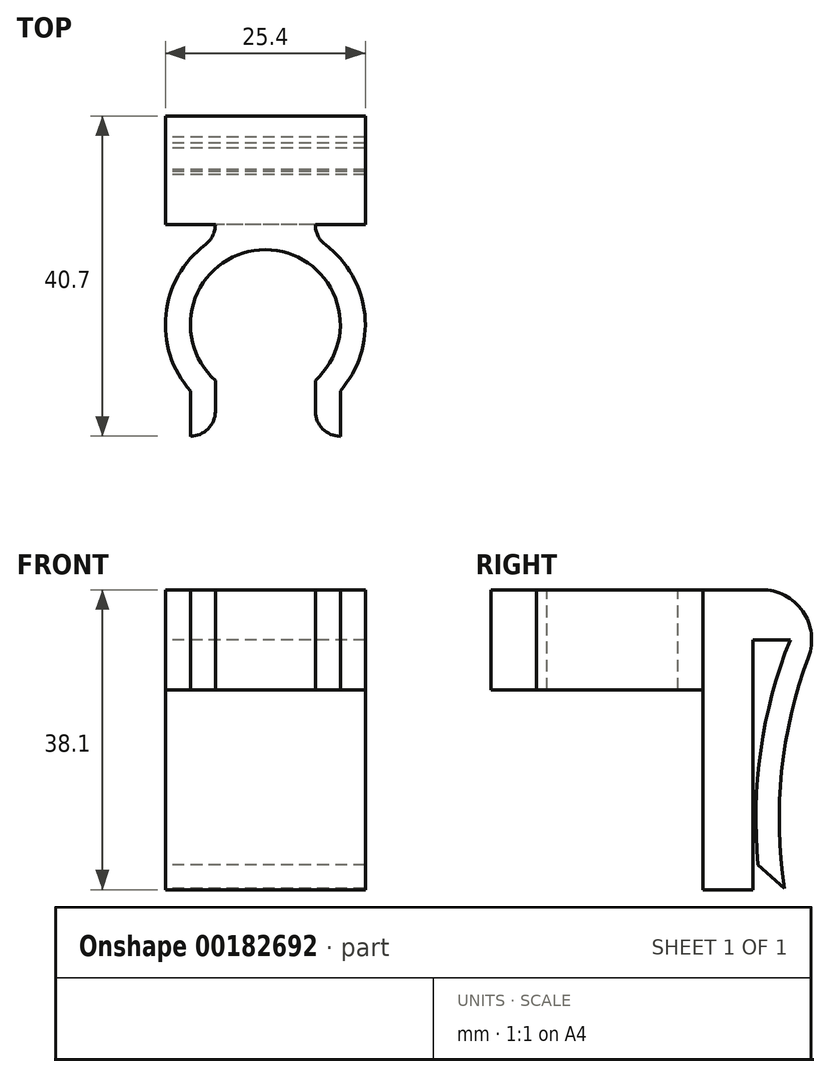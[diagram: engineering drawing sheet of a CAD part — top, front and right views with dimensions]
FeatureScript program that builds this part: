
annotation { "Feature Type Name" : "Feature", "Feature Type Description" : "" }
export const myFeature = defineFeature(function(context is Context, id is Id, definition is map)
    precondition{}
    {
        {
            var Q0;
            Q0=qCreatedBy(makeId("Right.planeOp"),FACE);
            var sketch = newSketch(context, id + "F0", { "sketchPlane" : qUnion([Q0])});
            skLineSegment(sketch, "E0", {"start": v(6.35, -44.45) * mm, "end": v(6.35, 6.35) * mm});
            skLineSegment(sketch, "E1", {"start": v(6.35, 6.35) * mm, "end": v(17.46, 6.35) * mm});
            skLineSegment(sketch, "E2", {"start": v(6.35, -44.45) * mm, "end": v(0, -44.45) * mm});
            skLineSegment(sketch, "E3", {"start": v(0, -44.45) * mm, "end": v(0, 6.35) * mm});
            skLineSegment(sketch, "E4", {"start": v(0, 6.35) * mm, "end": v(6.35, 6.35) * mm});
            skLineSegment(sketch, "E5", {"start": v(0, 0) * mm, "end": v(6.35, 0) * mm});
            skLineSegment(sketch, "E6", {"start": v(6.35, 0) * mm, "end": v(11.11, 0) * mm});
            skArc(sketch, "E7", {"start": v(11.11, 0) * mm, "mid": v(6.75, -22.19) * mm, "end": v(10.73, -44.45) * mm});
            skLineSegment(sketch, "E8", {"start": v(10.73, -44.45) * mm, "end": v(13.9, -44.45) * mm});
            skArc(sketch, "E9", {"start": v(17.46, 6.35) * mm, "mid": v(9.85, -18.64) * mm, "end": v(13.9, -44.45) * mm});
            skLineSegment(sketch, "E10", {"start": v(6.35, -44.45) * mm, "end": v(10.73, -44.45) * mm});
            skLineSegment(sketch, "E11", {"start": v(0, -31.75) * mm, "end": v(6.35, -31.75) * mm});
            skLineSegment(sketch, "E12", {"start": v(6.35, -31.75) * mm, "end": v(7.42, -31.75) * mm, "construction": true});
            skLineSegment(sketch, "E13", {"start": v(7.42, -31.75) * mm, "end": v(10.4, -31.75) * mm});
            skSolve(sketch);
        }
        {
            var Q0;
            {var subQ0=sQuery(id+"F0.wireOp",EDGE,"E4");Q0=makeQuery(id+"F0.imprint","IMPRINT",FACE,{"disambiguationData":[TD([[makeQuery(id+"F0.imprint","IMPRINT",EDGE,{"derivedFrom":subQ0}),-1.0]])]});}
            var Q1;
            {var subQ0=sQuery(id+"F0.wireOp",EDGE,"E5");Q1=makeQuery(id+"F0.imprint","IMPRINT",FACE,{"disambiguationData":[TD([[makeQuery(id+"F0.imprint","IMPRINT",EDGE,{"derivedFrom":subQ0}),-1.0]])]});}
            var Q2;
            {var subQ3=sQuery(id+"F0.wireOp",EDGE,"E1");Q2=makeQuery(id+"F0.imprint","IMPRINT",FACE,{"disambiguationData":[TD([[makeQuery(id+"F0.imprint","IMPRINT",EDGE,{"derivedFrom":subQ3}),-1.0]])]});}
            extrude(context, id + "F1", {"entities" : qUnion([Q0, Q1, Q2]), "depth" : 25.4 * mm});
        }
        {
            var Q0;
            Q0=makeQuery(id+"F1.opExtrude","SWEPT_FACE",FACE,{"disambiguationData":[OSD([sQuery(id+"F0.wireOp",EDGE,"E1"),sQuery(id+"F0.wireOp",EDGE,"E4")])]});
            var sketch = newSketch(context, id + "F2", { "sketchPlane" : qUnion([Q0])});
            skLineSegment(sketch, "E14", {"start": v(12.7, 0) * mm, "end": v(12.7, -12.7) * mm, "construction": true});
            skLineSegment(sketch, "E15", {"start": v(6.35, 0) * mm, "end": v(6.35, -1.7) * mm});
            skLineSegment(sketch, "E16", {"start": v(19.05, 0) * mm, "end": v(19.05, -1.7) * mm});
            skLineSegment(sketch, "E17", {"start": v(19.05, 0) * mm, "end": v(25.4, 0) * mm});
            skLineSegment(sketch, "E18", {"start": v(6.35, 0) * mm, "end": v(0, 0) * mm});
            skLineSegment(sketch, "E19", {"start": v(6.35, -23.7) * mm, "end": v(6.35, -26.87) * mm});
            skLineSegment(sketch, "E20", {"start": v(6.35, -26.87) * mm, "end": v(3.18, -26.87) * mm});
            skLineSegment(sketch, "E21", {"start": v(3.18, -26.87) * mm, "end": v(3.18, -21.1) * mm});
            skLineSegment(sketch, "E22.MirrorCS", {"start": v(22.23, -26.87) * mm, "end": v(22.23, -21.1) * mm});
            skLineSegment(sketch, "E23.MirrorCS", {"start": v(19.05, -23.7) * mm, "end": v(19.05, -26.87) * mm});
            skLineSegment(sketch, "E24.MirrorCS", {"start": v(19.05, -26.87) * mm, "end": v(22.23, -26.87) * mm});
            skLineSegment(sketch, "E25", {"start": v(6.35, -19.8) * mm, "end": v(6.35, -19.8) * mm});
            skLineSegment(sketch, "E26", {"start": v(6.35, -5.6) * mm, "end": v(6.35, -19.8) * mm, "construction": true});
            skLineSegment(sketch, "E27", {"start": v(6.35, -1.7) * mm, "end": v(6.35, -5.6) * mm, "construction": true});
            skArc(sketch, "E28", {"start": v(19.05, -1.7) * mm, "mid": v(15.99, -0.43) * mm, "end": v(12.7, 0) * mm, "construction": true});
            skArc(sketch, "E29", {"start": v(12.7, 0) * mm, "mid": v(9.41, -0.43) * mm, "end": v(6.35, -1.7) * mm, "construction": true});
            skArc(sketch, "E30", {"start": v(6.35, -1.7) * mm, "mid": v(0, -12.7) * mm, "end": v(6.35, -23.7) * mm});
            skLineSegment(sketch, "E31", {"start": v(19.05, -19.8) * mm, "end": v(19.05, -23.7) * mm});
            skLineSegment(sketch, "E32", {"start": v(19.05, -5.6) * mm, "end": v(19.05, -19.8) * mm, "construction": true});
            skLineSegment(sketch, "E33", {"start": v(6.35, -19.8) * mm, "end": v(6.35, -23.7) * mm});
            skArc(sketch, "E34", {"start": v(19.05, -19.8) * mm, "mid": v(12.7, -3.18) * mm, "end": v(6.35, -19.8) * mm});
            skArc(sketch, "E35", {"start": v(6.35, -19.8) * mm, "mid": v(12.7, -22.23) * mm, "end": v(19.05, -19.8) * mm, "construction": true});
            skArc(sketch, "E36", {"start": v(6.35, -23.7) * mm, "mid": v(12.7, -25.4) * mm, "end": v(19.05, -23.7) * mm, "construction": true});
            skArc(sketch, "E37", {"start": v(19.05, -23.7) * mm, "mid": v(25.4, -12.7) * mm, "end": v(19.05, -1.7) * mm});
            skLineSegment(sketch, "E38", {"start": v(19.05, -1.7) * mm, "end": v(19.05, -1.7) * mm});
            skLineSegment(sketch, "E39", {"start": v(19.05, -5.6) * mm, "end": v(19.05, -5.6) * mm});
            skLineSegment(sketch, "E40", {"start": v(19.05, -1.7) * mm, "end": v(19.05, -5.6) * mm, "construction": true});
            skSolve(sketch);
        }
        {
            var Q0;
            {var subQ3=sQuery(id+"F2.wireOp",EDGE,"E15");Q0=makeQuery(id+"F2.imprint","IMPRINT",FACE,{"disambiguationData":[TD([[makeQuery(id+"F2.imprint","IMPRINT",EDGE,{"derivedFrom":subQ3}),1.0]])]});}
            var Q1;
            {var subQ0=sQuery(id+"F2.wireOp",EDGE,"E19");Q1=makeQuery(id+"F2.imprint","IMPRINT",FACE,{"disambiguationData":[TD([[makeQuery(id+"F2.imprint","IMPRINT",EDGE,{"derivedFrom":subQ0}),-1.0]])]});}
            var Q2;
            Q2=makeQuery(id+"F2.imprint","IMPRINT",FACE,{"disambiguationData":[TD([[makeQuery(id+"F2.imprint","IMPRINT",EDGE,{"derivedFrom":sQuery(id+"F2.wireOp",EDGE,"E24.MirrorCS")}),1.0]])]});
            var Q3;
            Q3=sQuery(id+"F2.wireOp",EDGE,"E40");
            extrude(context, id + "F3", {"entities" : qUnion([Q0, Q1, Q2]), "operationType" : NewBodyOperationType.ADD, "surfaceEntities" : qUnion([Q3]), "oppositeDirection" : true, "depth" : 12.7 * mm});
        }
        {
            var Q0;
            Q0=makeQuery(id+"F3.opExtrude","SWEPT_EDGE",EDGE,{"disambiguationData":[OSD([sQuery(id+"F2.wireOp",EDGE,"E19"),sQuery(id+"F2.wireOp",EDGE,"E20")])]});
            var Q1;
            Q1=makeQuery(id+"F3.opExtrude","SWEPT_EDGE",EDGE,{"disambiguationData":[OSD([sQuery(id+"F2.wireOp",EDGE,"E24.MirrorCS"),sQuery(id+"F2.wireOp",EDGE,"E23.MirrorCS")])]});
            fillet(context, id + "F4", {"entities" : qUnion([Q0, Q1]), "radius" : 3.17 * mm, "tangentPropagation" : true, "allowEdgeOverflow" : false});
        }
        {
            var Q0;
            Q0=makeQuery(id+"F3.opExtrude","SWEPT_EDGE",EDGE,{"disambiguationData":[OSD([sQuery(id+"F0.wireOp",EDGE,"E3"),sQuery(id+"F0.wireOp",EDGE,"E4"),sQuery(id+"F2.wireOp",EDGE,"E16"),sQuery(id+"F2.wireOp",EDGE,"E17")])]});
            var Q1;
            Q1=makeQuery(id+"F3.opExtrude","SWEPT_EDGE",EDGE,{"disambiguationData":[OSD([sQuery(id+"F0.wireOp",EDGE,"E3"),sQuery(id+"F0.wireOp",EDGE,"E4"),sQuery(id+"F2.wireOp",EDGE,"E15"),sQuery(id+"F2.wireOp",EDGE,"E18")])]});
            var Q2;
            Q2=makeQuery(id+"F3.opExtrude","SWEPT_EDGE",EDGE,{"disambiguationData":[OSD([sQuery(id+"F2.wireOp",EDGE,"E15"),sQuery(id+"F2.wireOp",EDGE,"E30")])]});
            var Q3;
            Q3=makeQuery(id+"F3.opExtrude","SWEPT_EDGE",EDGE,{"disambiguationData":[OSD([sQuery(id+"F2.wireOp",EDGE,"E16"),sQuery(id+"F2.wireOp",EDGE,"E37")])]});
            fillet(context, id + "F5", {"entities" : qUnion([Q0, Q1, Q2, Q3]), "radius" : 3.17 * mm, "tangentPropagation" : true, "allowEdgeOverflow" : false});
        }
        {
            var Q0;
            Q0=makeQuery(id+"F1.opExtrude","SWEPT_EDGE",EDGE,{"disambiguationData":[OSD([sQuery(id+"F0.wireOp",EDGE,"E1"),sQuery(id+"F0.wireOp",EDGE,"E9")])]});
            fillet(context, id + "F6", {"entities" : qUnion([Q0]), "radius" : 6.35 * mm, "tangentPropagation" : true, "allowEdgeOverflow" : false});
        }
        {
            var Q0;
            Q0=makeQuery(id+"F1.opExtrude","SWEPT_EDGE",EDGE,{"disambiguationData":[OSD([sQuery(id+"F0.wireOp",EDGE,"E7"),sQuery(id+"F0.wireOp",EDGE,"E13")])]});
            chamfer(context, id + "F7", {"entities" : qUnion([Q0]), "width" : 3.17 * mm, "tangentPropagation" : true});
        }
    });
